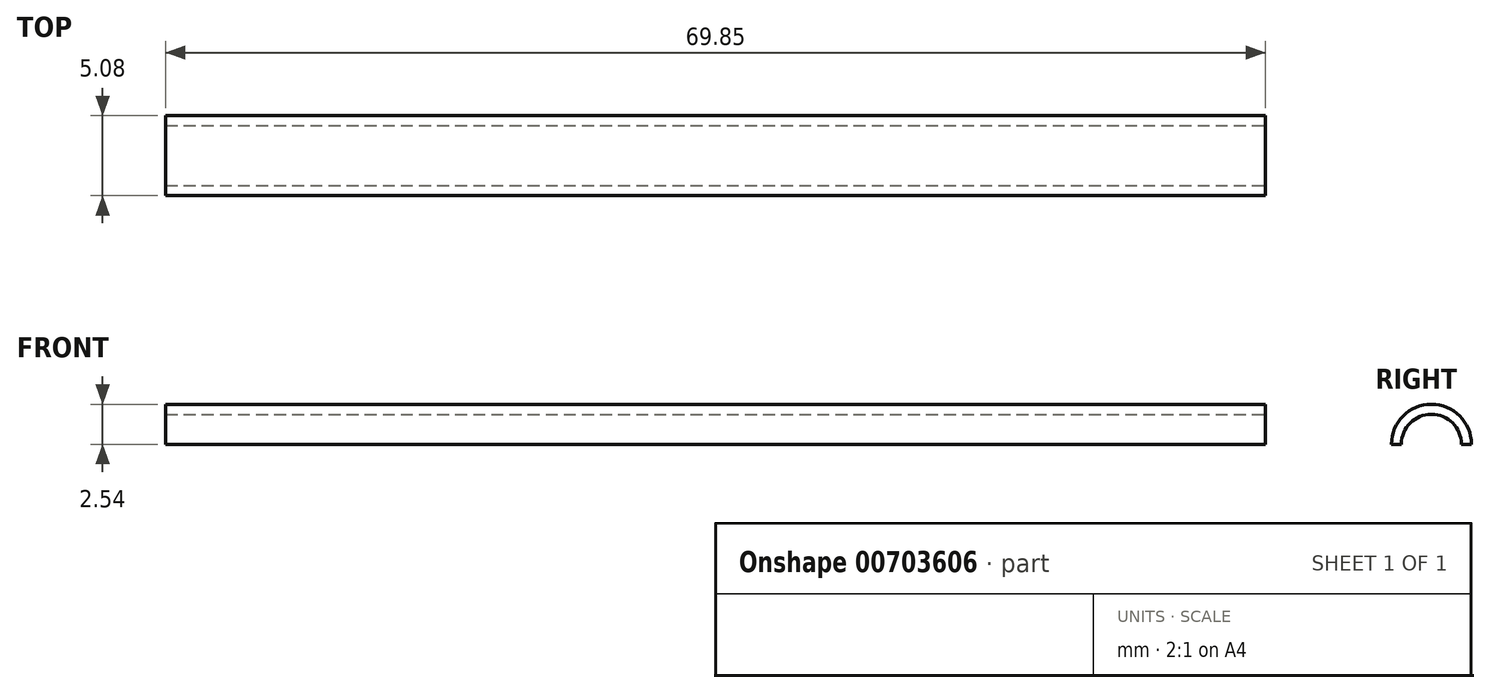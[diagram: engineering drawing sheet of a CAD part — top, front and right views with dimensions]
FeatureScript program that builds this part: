
annotation { "Feature Type Name" : "Feature", "Feature Type Description" : "" }
export const myFeature = defineFeature(function(context is Context, id is Id, definition is map)
    precondition{}
    {
        {
            var Q0;
            Q0=qCreatedBy(makeId("Top.planeOp"),FACE);
            var sketch = newSketch(context, id + "F0", { "sketchPlane" : qUnion([Q0])});
            skLineSegment(sketch, "E0.bottom", {"start": v(-75, 51.47) * mm, "end": v(-5.14, 51.47) * mm});
            skLineSegment(sketch, "E0.top", {"start": v(-75, 46.4) * mm, "end": v(-5.14, 46.4) * mm});
            skLineSegment(sketch, "E0.left", {"start": v(-75, 51.47) * mm, "end": v(-75, 46.4) * mm});
            skLineSegment(sketch, "E0.right", {"start": v(-5.14, 51.47) * mm, "end": v(-5.14, 46.4) * mm});
            skSolve(sketch);
        }
        {
            var Q0;
            Q0=makeQuery(id+"F0.imprint","IMPRINT",FACE,{"disambiguationData":[TD([[makeQuery(id+"F0.imprint","IMPRINT",EDGE,{"derivedFrom":sQuery(id+"F0.wireOp",EDGE,"E0.bottom")}),-1.0]])]});
            extrude(context, id + "F1", {"entities" : qUnion([Q0]), "depth" : 2.54 * mm, "offsetDistance" : 25.4 * mm});
        }
        {
            var Q0;
            Q0=makeQuery(id+"F1.opExtrude","CAP_EDGE",EDGE,{"disambiguationData":[OSD([sQuery(id+"F0.wireOp",EDGE,"E0.top")])],"isStart":false});
            var Q1;
            Q1=makeQuery(id+"F1.opExtrude","CAP_EDGE",EDGE,{"disambiguationData":[OSD([sQuery(id+"F0.wireOp",EDGE,"E0.bottom")])],"isStart":false});
            fillet(context, id + "F2", {"entities" : qUnion([Q0, Q1]), "radius" : 2.54 * mm, "tangentPropagation" : true, "allowEdgeOverflow" : false});
        }
        {
            var Q0;
            Q0=makeQuery(id+"F1.opExtrude","SWEPT_FACE",FACE,{"disambiguationData":[OSD([sQuery(id+"F0.wireOp",EDGE,"E0.right")])]});
            var sketch = newSketch(context, id + "F3", { "sketchPlane" : qUnion([Q0])});
            skCircle(sketch, "E1", {"center": v(48.93, 0) * mm, "radius": 1.59 * mm});
            skSolve(sketch);
        }
        {
            var Q0;
            Q0=sQuery(id+"F3.wireOp",VERTEX,"E1.center");
            var Q1;
            Q1=makeQuery(id+"F1.opExtrude","SWEPT_BODY",BODY,{"disambiguationData":[OSD([sQuery(id+"F0.wireOp",EDGE,"E0.bottom"),sQuery(id+"F0.wireOp",EDGE,"E0.top"),sQuery(id+"F0.wireOp",EDGE,"E0.left"),sQuery(id+"F0.wireOp",EDGE,"E0.right")])]});
            hole(context, id + "F4", {"style" : HoleStyle.SIMPLE, "endStyle" : HoleEndStyle.THROUGH, "holeDiameter" : 3.8 * mm, "majorDiameter" : 6.35 * mm, "isTappedThrough" : true, "tappedDepth" : 12.7 * mm, "tapClearance" : 3, "locations" : qUnion([Q0]), "scope" : qUnion([Q1])});
        }
    });
